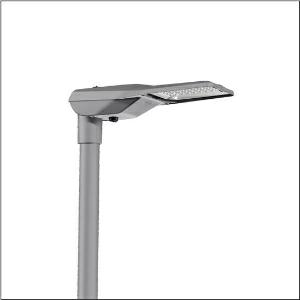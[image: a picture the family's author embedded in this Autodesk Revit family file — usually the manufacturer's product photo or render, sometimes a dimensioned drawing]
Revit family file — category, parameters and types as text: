
# Revit family: streetlight_sl_21_iq_mini___st0_5a_5xe2b31y08jb_a8c8
name_source: partatom
category: Lighting Fixtures
units: mm (PartAtom-declared; Revit-internal decimal feet)

## family parameters
Cut with Voids When Loaded = No
Host = Face
Light Source = No
Part Type = Normal
Room Calculation Point = No
Round Connector Dimension = Use Diameter
Shared = No

## types (1)
- --- (1 x LED, 11210 lm, 72.5 W, 3000K)
    Apparent Load = 73 VA
    CIE Flux Codes = 43 76 97 100 100
    Color Rendering = 70
    Color Temperature = 3000K
    Default Elevation = 1800 mm
    Description = Streetlight SL 21 iQ mini, mast luminaire, primary light control with lens, of PMMA, primary optical cover: cover, of toughened safety glass, transparent, light distribution: ST0.5a, light emission: direct distribution, primary light characteristic: asymmetric, installation type: post-top, side-entry, LED, High Power LED, rated luminous flux: 11.210lm, luminous efficacy: 155lm/W, light colour: 730, colour temperature: 3000K, control: presetting dimming logarithmic, Street-Remote, Auto-Match, Temp-Guard, Lumen-Switch, Night-Set, Smart-Wire, Light-Fading, Desk-Remote (wireless, voltage-free reading and setting of iQ features in the workshop via application-optimized NFC function/RFID function), optimised constant luminous flux control (CLO 2.0), mains connection: 220..240V, AC, 50/60Hz, start of lifetime: 73W, end of service life: 76W, reduction: 33W, luminaire housing, of diecast aluminium, powder-coated, Siteco® metallic grey (DB 702S), corrosivity category C5 mid according to DIN EN ISO 12944, please order mast flange separately, inclination adjustable: 0°, 5°, 10°, 15°, sealing non-destructively replaceable, multi-level sealing system, length: 628mm, width: 235mm, height: 110mm, mast flange for spigot size: 42mm (side-entry): 5XC10008XM4, 60/48mm (side-entry/post-top): 5XC10108XM2, 76/60mm (side-entry/post-top): 5XC10108XM1, Smart Interface below and above, protection rating (complete): IP66, insulation class (complete): insulation class II (safety insulation), certification: CE, ENEC, ENEC+, VDE, impact resistance: IK09, permissible operating ambient temperature for outdoor applications: -40..+50°C, standard-compliant lighting for roads and squares, packaging unit: 1 piece

Light Distribution: ST0.5a
    Height = 110 mm
    Lamp = 1 x LED
    Lamp Light Flux = 11210 lm
    Lamp Power = 72.5 W
    Lamp count = 1
    Length = 625 mm
    Luminous efficacy = 155 lm/W
    Manufacturer = Siteco
    ModVariant = No
    Model = 5XE2B31Y08JB
    Number of Poles = 1
    OnlyDefault = Yes
    Power Factor = 1
    Product Name = Streetlight SL 21 iQ mini | ST0.5a
    Product group = mast luminaire | pylon top
    ProductGroupID = 6100
    Protection Class = Protection class II
    Protection Degree = IP 66
    RLX_Detail_Level = 1
    RLX_Emergency_Light_Flux = 0 lm
    RLX_Emergency_Type = 0
    RLX_Emergency_Type_DB = No
    RlxData = <blob elided: 103769 chars, md5=9159e1d6>
    Socket = socket
    Standby Power = 0 W
    System Light Flux = 11210 lm
    System Power = 73 W
    Type Comments = factory setting: luminous flux: 100 % | dim-lin: 254 | 755 mA
    Type Image = l_1003514.jpg
    URL = http://relux.com
    VarID = @adj_045875
    Voltage = 0 V
    Weight = 0.00 kg
    Width = 234 mm

## geometry (parser evidence)
native form markers: Blend x4, Sweep x9
no freeform markers — native parametric forms only
